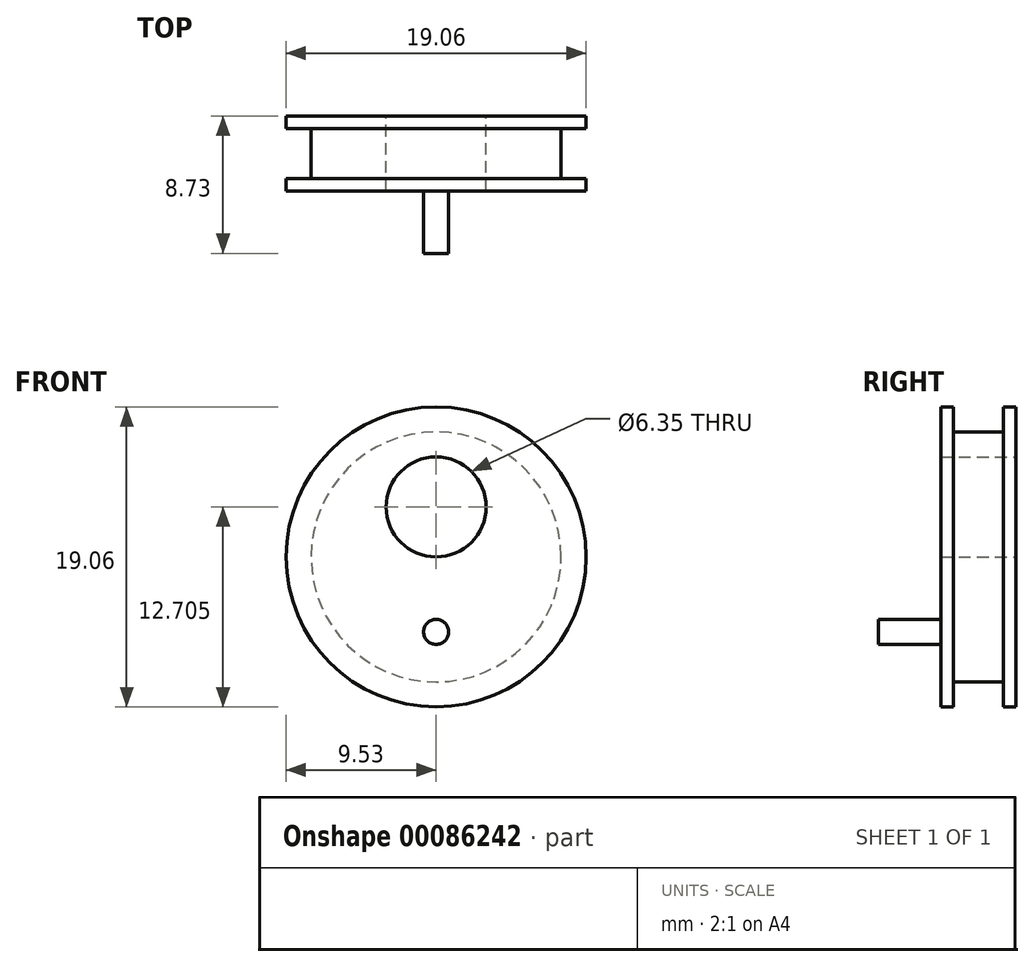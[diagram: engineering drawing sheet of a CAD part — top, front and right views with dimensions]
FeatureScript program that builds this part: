
annotation { "Feature Type Name" : "Feature", "Feature Type Description" : "" }
export const myFeature = defineFeature(function(context is Context, id is Id, definition is map)
    precondition{}
    {
        {
            var Q0;
            Q0=qCreatedBy(makeId("Right.planeOp"),FACE);
            var sketch = newSketch(context, id + "F0", { "sketchPlane" : qUnion([Q0])});
            skLineSegment(sketch, "E0", {"start": v(-2.38, 0) * mm, "end": v(-2.38, 9.52) * mm});
            skLineSegment(sketch, "E1", {"start": v(-2.38, 9.52) * mm, "end": v(-1.59, 9.52) * mm});
            skLineSegment(sketch, "E2", {"start": v(-1.59, 9.52) * mm, "end": v(-1.59, 7.94) * mm});
            skLineSegment(sketch, "E3", {"start": v(-1.59, 7.94) * mm, "end": v(1.59, 7.94) * mm});
            skLineSegment(sketch, "E4", {"start": v(1.59, 7.94) * mm, "end": v(1.59, 9.52) * mm});
            skLineSegment(sketch, "E5", {"start": v(1.59, 9.52) * mm, "end": v(2.38, 9.52) * mm});
            skLineSegment(sketch, "E6", {"start": v(2.38, 9.52) * mm, "end": v(2.38, 0) * mm});
            skLineSegment(sketch, "E7", {"start": v(2.38, 0) * mm, "end": v(0, 0) * mm});
            skLineSegment(sketch, "E8", {"start": v(0, 0) * mm, "end": v(-2.38, 0) * mm});
            skLineSegment(sketch, "E9", {"start": v(-2.38, 0) * mm, "end": v(-2.38, -9.52) * mm, "construction": true});
            skLineSegment(sketch, "E10", {"start": v(-2.38, -9.52) * mm, "end": v(-1.59, -9.52) * mm, "construction": true});
            skLineSegment(sketch, "E11", {"start": v(-1.59, -9.52) * mm, "end": v(-1.59, -7.94) * mm, "construction": true});
            skLineSegment(sketch, "E12", {"start": v(-1.59, -7.94) * mm, "end": v(1.59, -7.94) * mm, "construction": true});
            skLineSegment(sketch, "E13", {"start": v(1.59, -7.94) * mm, "end": v(1.59, -9.52) * mm, "construction": true});
            skLineSegment(sketch, "E14", {"start": v(1.59, -9.52) * mm, "end": v(2.38, -9.52) * mm, "construction": true});
            skLineSegment(sketch, "E15", {"start": v(2.38, -9.52) * mm, "end": v(2.38, 0) * mm, "construction": true});
            skSolve(sketch);
        }
        {
            var Q0;
            Q0=makeQuery(id+"F0.imprint","IMPRINT",FACE,{"disambiguationData":[TD([[makeQuery(id+"F0.imprint","IMPRINT",EDGE,{"derivedFrom":sQuery(id+"F0.wireOp",EDGE,"E0")}),-1.0]])]});
            var Q1;
            Q1=sQuery(id+"F0.wireOp",EDGE,"E7");
            revolve(context, id + "F1", {"entities" : qUnion([Q0]), "axis" : qUnion([Q1]), "revolveType" : RevolveType.FULL});
        }
        {
            var Q0;
            Q0=makeQuery(id+"F1.opRevolve","SWEPT_FACE",FACE,{"disambiguationData":[OSD([sQuery(id+"F0.wireOp",EDGE,"E0")])]});
            var sketch = newSketch(context, id + "F2", { "sketchPlane" : qUnion([Q0])});
            skPoint(sketch, "E16", {"position": v(0, 3.17) * mm});
            skSolve(sketch);
        }
        {
            var Q0;
            Q0=sQuery(id+"F2.wireOp",VERTEX,"E16");
            var Q1;
            Q1=makeQuery(id+"F1.opRevolve","SWEPT_BODY",BODY,{"disambiguationData":[OSD([sQuery(id+"F0.wireOp",EDGE,"E0"),sQuery(id+"F0.wireOp",EDGE,"E1"),sQuery(id+"F0.wireOp",EDGE,"E2"),sQuery(id+"F0.wireOp",EDGE,"E3"),sQuery(id+"F0.wireOp",EDGE,"E4"),sQuery(id+"F0.wireOp",EDGE,"E5"),sQuery(id+"F0.wireOp",EDGE,"E6"),sQuery(id+"F0.wireOp",EDGE,"E7"),sQuery(id+"F0.wireOp",EDGE,"E8")])]});
            hole(context, id + "F3", {"style" : HoleStyle.SIMPLE, "endStyle" : HoleEndStyle.THROUGH, "holeDiameter" : 6.35 * mm, "locations" : qUnion([Q0]), "scope" : qUnion([Q1]), "isTappedThrough" : true});
        }
        {
            var Q0;
            Q0=makeQuery(id+"F1.opRevolve","SWEPT_FACE",FACE,{"disambiguationData":[OSD([sQuery(id+"F0.wireOp",EDGE,"E0")])]});
            var sketch = newSketch(context, id + "F4", { "sketchPlane" : qUnion([Q0])});
            skCircle(sketch, "E17", {"center": v(0, -4.76) * mm, "radius": 0.8 * mm});
            skSolve(sketch);
        }
        {
            var Q0;
            Q0 = qSketchRegion(id + "F4", true);
            extrude(context, id + "F5", {"entities" : qUnion([Q0]), "operationType" : NewBodyOperationType.ADD, "depth" : ((5 / 32) * 25.4) * mm});
        }
    });
